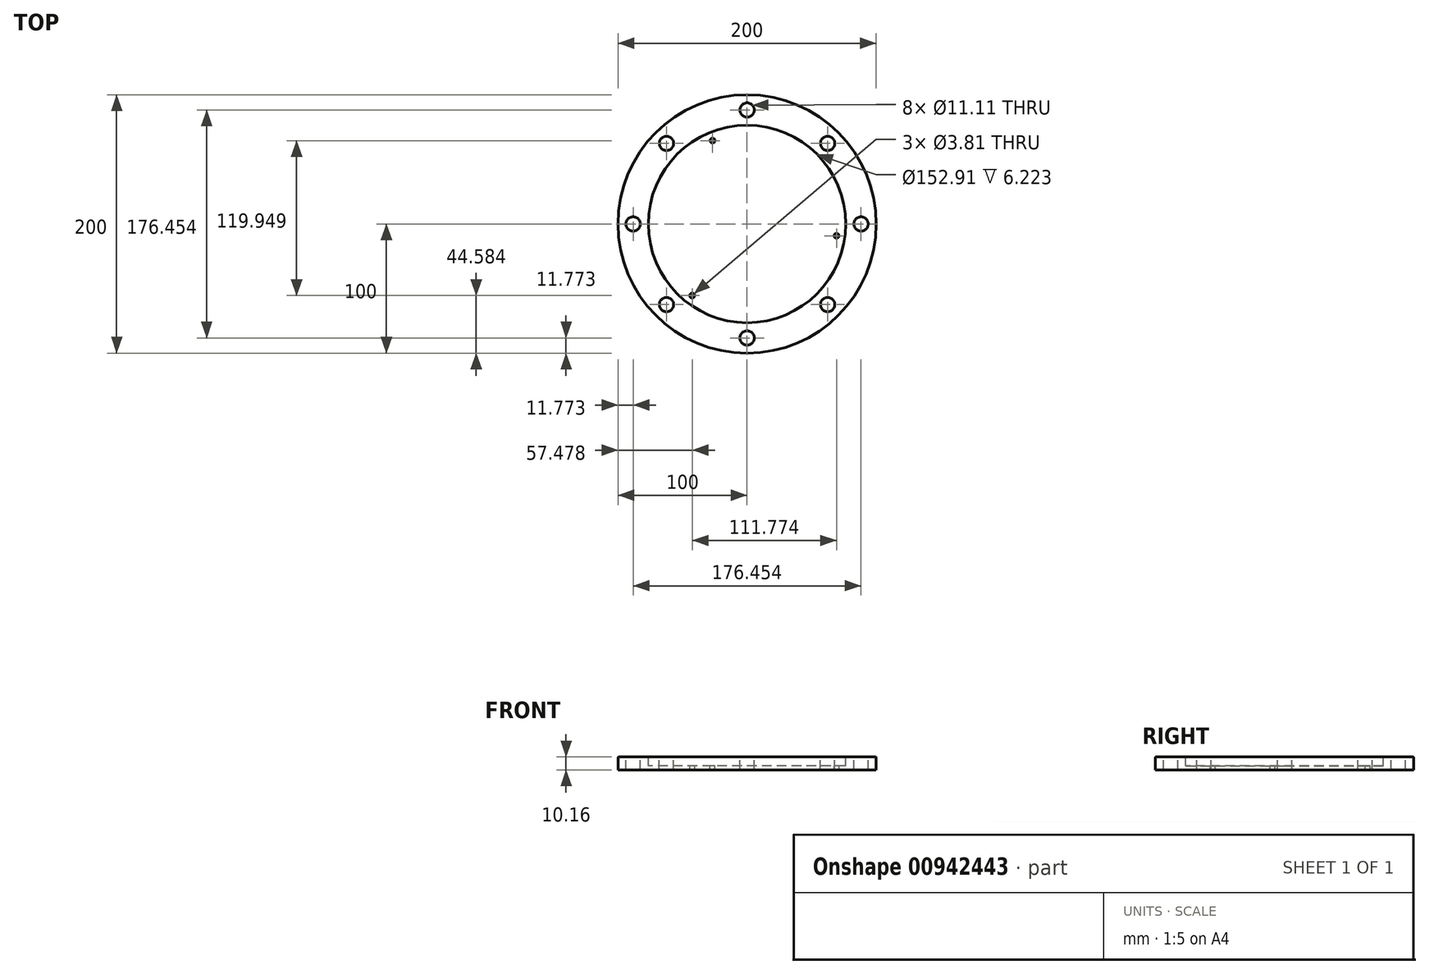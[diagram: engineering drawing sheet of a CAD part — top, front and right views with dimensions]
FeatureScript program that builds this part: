
annotation { "Feature Type Name" : "Feature", "Feature Type Description" : "" }
export const myFeature = defineFeature(function(context is Context, id is Id, definition is map)
    precondition{}
    {
        {
            var Q0;
            Q0=qCreatedBy(makeId("Front.planeOp"),FACE);
            var sketch = newSketch(context, id + "F0", { "sketchPlane" : qUnion([Q0])});
            skLineSegment(sketch, "E0", {"start": v(0, 171.73) * mm, "end": v(0, 0) * mm, "construction": true});
            skLineSegment(sketch, "E1", {"start": v(0, 0) * mm, "end": v(100, 0) * mm});
            skLineSegment(sketch, "E2", {"start": v(100, 0) * mm, "end": v(100, 9.4) * mm});
            skLineSegment(sketch, "E3", {"start": v(0, 0) * mm, "end": v(0, 9.53) * mm});
            skLineSegment(sketch, "E4", {"start": v(0, 9.53) * mm, "end": v(76.45, 9.53) * mm});
            skLineSegment(sketch, "E5", {"start": v(76.45, 9.4) * mm, "end": v(76.45, 9.53) * mm});
            skLineSegment(sketch, "E6", {"start": v(77.22, 10.16) * mm, "end": v(99.24, 10.16) * mm});
            skPoint(sketch, "E7.visualSharp", {"position": v(100, 10.16) * mm});
            skArc(sketch, "E7.filletArc", {"start": v(100, 9.4) * mm, "mid": v(99.78, 9.94) * mm, "end": v(99.24, 10.16) * mm});
            skPoint(sketch, "E8.visualSharp", {"position": v(76.45, 10.16) * mm});
            skArc(sketch, "E8.filletArc", {"start": v(77.22, 10.16) * mm, "mid": v(76.68, 9.94) * mm, "end": v(76.45, 9.4) * mm});
            skSolve(sketch);
        }
        {
            var Q0;
            Q0=makeQuery(id+"F0.imprint","IMPRINT",FACE,{"disambiguationData":[TD([[makeQuery(id+"F0.imprint","IMPRINT",EDGE,{"derivedFrom":sQuery(id+"F0.wireOp",EDGE,"E1")}),1.0]])]});
            var Q1;
            Q1 = qConstructionFilter(qBodyType(qCreatedBy(id + "F0" ,EDGE), BodyType.WIRE), ConstructionObject.NO);
            var Q2;
            Q2=sQuery(id+"F0.wireOp",EDGE,"E0");
            revolve(context, id + "F1", {"surfaceOperationType" : NewSurfaceOperationType.NEW, "entities" : qUnion([Q0]), "surfaceEntities" : qUnion([Q1]), "axis" : qUnion([Q2]), "revolveType" : RevolveType.FULL});
        }
        {
            var Q0;
            Q0=makeQuery(id+"F1.opRevolve","SWEPT_FACE",FACE,{"disambiguationData":[OSD([sQuery(id+"F0.wireOp",EDGE,"E4")])]});
            var sketch = newSketch(context, id + "F2", { "sketchPlane" : qUnion([Q0])});
            skCircle(sketch, "E9", {"center": v(0, 0) * mm, "radius": 76.45 * mm});
            skSolve(sketch);
        }
        {
            var Q0;
            Q0 = qSketchRegion(id + "F2", true);
            extrude(context, id + "F3", {"entities" : qUnion([Q0]), "operationType" : NewBodyOperationType.REMOVE, "oppositeDirection" : true, "depth" : 6.35 * mm, "offsetDistance" : 25.4 * mm});
        }
        {
            var Q0;
            Q0=makeQuery(id+"F1.opRevolve","SWEPT_FACE",FACE,{"disambiguationData":[OSD([sQuery(id+"F0.wireOp",EDGE,"E6")])]});
            var sketch = newSketch(context, id + "F4", { "sketchPlane" : qUnion([Q0])});
            skCircle(sketch, "E10", {"center": v(0, 88.23) * mm, "radius": 5.56 * mm});
            skLineSegment(sketch, "E11", {"start": v(0, 76.45) * mm, "end": v(0, 100) * mm, "construction": true});
            skCircle(sketch, "E12.1.0", {"center": v(-62.39, 62.39) * mm, "radius": 5.56 * mm});
            skCircle(sketch, "E12.2.0", {"center": v(-88.23, 0) * mm, "radius": 5.56 * mm});
            skCircle(sketch, "E12.3.0", {"center": v(-62.39, -62.39) * mm, "radius": 5.56 * mm});
            skCircle(sketch, "E12.4.0", {"center": v(0, -88.23) * mm, "radius": 5.56 * mm});
            skCircle(sketch, "E12.5.0", {"center": v(62.39, -62.39) * mm, "radius": 5.56 * mm});
            skCircle(sketch, "E12.6.0", {"center": v(88.23, 0) * mm, "radius": 5.56 * mm});
            skCircle(sketch, "E12.7.0", {"center": v(62.39, 62.39) * mm, "radius": 5.56 * mm});
            skPoint(sketch, "E12.center", {"position": v(0, 0) * mm});
            skSolve(sketch);
        }
        {
            var Q0;
            Q0 = qSketchRegion(id + "F4", true);
            extrude(context, id + "F5", {"entities" : qUnion([Q0]), "operationType" : NewBodyOperationType.REMOVE, "endBound" : BoundingType.THROUGH_ALL, "oppositeDirection" : true, "depth" : 25.4 * mm, "offsetDistance" : 25.4 * mm});
        }
        {
            var Q0;
            Q0=makeQuery(id+"F3.boolean.opBoolean","COPY",FACE,{"derivedFrom":makeQuery(id+"F3.opExtrude","CAP_FACE",FACE,{"disambiguationData":[OSD([sQuery(id+"F2.wireOp",EDGE,"E9")])],"isStart":false})});
            var sketch = newSketch(context, id + "F6", { "sketchPlane" : qUnion([Q0])});
            skCircle(sketch, "E13", {"center": v(-26.73, 64.53) * mm, "radius": 1.9 * mm});
            skCircle(sketch, "E14.1.0", {"center": v(-42.52, -55.42) * mm, "radius": 1.9 * mm});
            skCircle(sketch, "E14.2.0", {"center": v(69.25, -9.12) * mm, "radius": 1.9 * mm});
            skPoint(sketch, "E14.center", {"position": v(0, 0) * mm});
            skLineSegment(sketch, "E15", {"start": v(-26.73, 64.53) * mm, "end": v(0, 0) * mm, "construction": true});
            skSolve(sketch);
        }
        {
            var Q0;
            Q0 = qSketchRegion(id + "F6", true);
            extrude(context, id + "F7", {"entities" : qUnion([Q0]), "operationType" : NewBodyOperationType.REMOVE, "endBound" : BoundingType.THROUGH_ALL, "oppositeDirection" : true, "depth" : 25.4 * mm, "offsetDistance" : 25.4 * mm});
        }
    });
